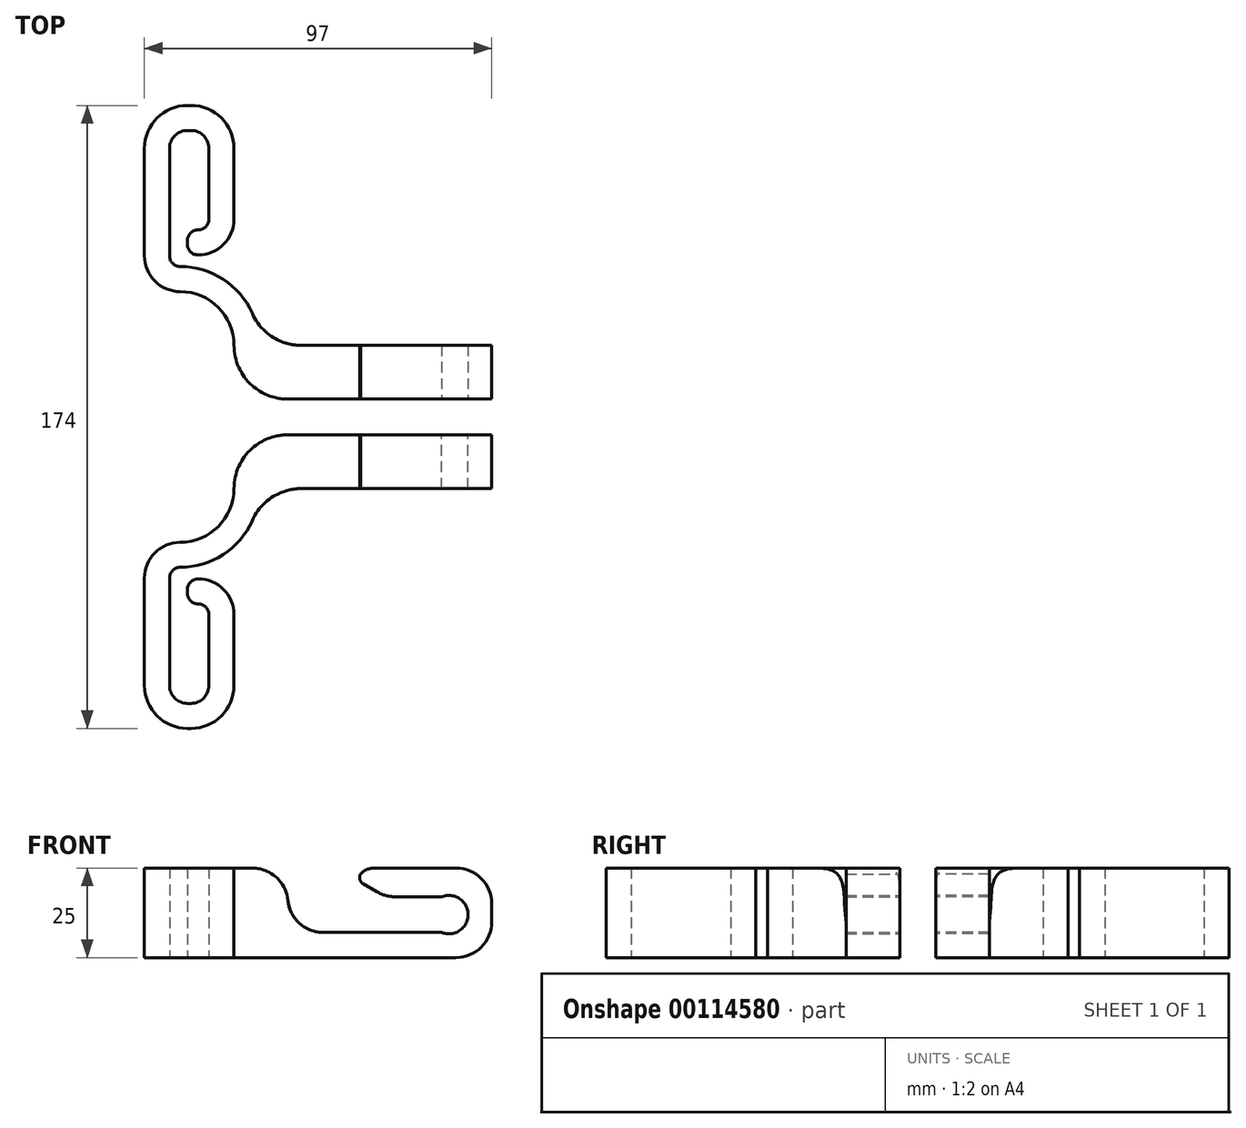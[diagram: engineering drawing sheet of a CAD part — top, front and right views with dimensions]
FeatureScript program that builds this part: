
annotation { "Feature Type Name" : "Feature", "Feature Type Description" : "" }
export const myFeature = defineFeature(function(context is Context, id is Id, definition is map)
    precondition{}
    {
        {
            var Q0;
            Q0=qCreatedBy(makeId("Top.planeOp"),FACE);
            var sketch = newSketch(context, id + "F0", { "sketchPlane" : qUnion([Q0])});
            skLineSegment(sketch, "E0", {"start": v(0, 15) * mm, "end": v(0, 15) * mm});
            skLineSegment(sketch, "E1", {"start": v(-15, 30) * mm, "end": v(-15, 30) * mm});
            skLineSegment(sketch, "E2", {"start": v(-25, 40) * mm, "end": v(-25, 70) * mm});
            skLineSegment(sketch, "E3", {"start": v(-13, 82) * mm, "end": v(-12, 82) * mm});
            skLineSegment(sketch, "E4", {"start": v(15, 0) * mm, "end": v(72, 0) * mm});
            skLineSegment(sketch, "E5", {"start": v(72, 0) * mm, "end": v(72, 15) * mm});
            skPoint(sketch, "E6.visualSharp", {"position": v(0, 30) * mm});
            skArc(sketch, "E6.filletArc", {"start": v(0, 15) * mm, "mid": v(-4.4, 25.6) * mm, "end": v(-15, 30) * mm});
            skLineSegment(sketch, "E7", {"start": v(0, 70) * mm, "end": v(0, 50.23) * mm});
            skLineSegment(sketch, "E8", {"start": v(-10, 40.23) * mm, "end": v(-10, 40.23) * mm});
            skPoint(sketch, "E9.visualSharp", {"position": v(-25, 30) * mm});
            skArc(sketch, "E9.filletArc", {"start": v(-25, 40) * mm, "mid": v(-22.07, 32.93) * mm, "end": v(-15, 30) * mm});
            skPoint(sketch, "E10.visualSharp", {"position": v(0, 40.23) * mm});
            skArc(sketch, "E10.filletArc", {"start": v(-10, 40.23) * mm, "mid": v(-2.93, 43.16) * mm, "end": v(0, 50.23) * mm});
            skPoint(sketch, "E11.visualSharp", {"position": v(0, 82) * mm});
            skArc(sketch, "E11.filletArc", {"start": v(0, 70) * mm, "mid": v(-3.51, 78.49) * mm, "end": v(-12, 82) * mm});
            skPoint(sketch, "E12.visualSharp", {"position": v(-25, 82) * mm});
            skArc(sketch, "E12.filletArc", {"start": v(-13, 82) * mm, "mid": v(-21.49, 78.49) * mm, "end": v(-25, 70) * mm});
            skArc(sketch, "E13.0", {"start": v(5.11, 23.92) * mm, "mid": v(-3, 33.44) * mm, "end": v(-15, 37) * mm});
            skArc(sketch, "E13.1", {"start": v(-18, 40) * mm, "mid": v(-17.12, 37.88) * mm, "end": v(-15, 37) * mm});
            skLineSegment(sketch, "E13.2", {"start": v(-18, 40) * mm, "end": v(-18, 70) * mm});
            skArc(sketch, "E13.3", {"start": v(-13, 75) * mm, "mid": v(-16.54, 73.54) * mm, "end": v(-18, 70) * mm});
            skLineSegment(sketch, "E13.4", {"start": v(-13, 75) * mm, "end": v(-12, 75) * mm});
            skLineSegment(sketch, "E13.5", {"start": v(-10, 47.23) * mm, "end": v(-10, 47.23) * mm});
            skArc(sketch, "E13.6", {"start": v(-10, 47.23) * mm, "mid": v(-7.88, 48.11) * mm, "end": v(-7, 50.23) * mm});
            skLineSegment(sketch, "E13.7", {"start": v(-7, 70) * mm, "end": v(-7, 50.23) * mm});
            skArc(sketch, "E13.8", {"start": v(-7, 70) * mm, "mid": v(-8.46, 73.54) * mm, "end": v(-12, 75) * mm});
            skLineSegment(sketch, "E14", {"start": v(-13, 44.23) * mm, "end": v(-13, 43.23) * mm});
            skPoint(sketch, "E15.visualSharp", {"position": v(-13, 47.23) * mm});
            skArc(sketch, "E15.filletArc", {"start": v(-10, 47.23) * mm, "mid": v(-12.12, 46.35) * mm, "end": v(-13, 44.23) * mm});
            skPoint(sketch, "E16.visualSharp", {"position": v(-13, 40.23) * mm});
            skArc(sketch, "E16.filletArc", {"start": v(-13, 43.23) * mm, "mid": v(-12.12, 41.11) * mm, "end": v(-10, 40.23) * mm});
            skLineSegment(sketch, "E17", {"start": v(72, 15) * mm, "end": v(18.82, 15) * mm});
            skPoint(sketch, "E18.visualSharp", {"position": v(0, 0) * mm});
            skArc(sketch, "E18.filletArc", {"start": v(0, 15) * mm, "mid": v(4.4, 4.4) * mm, "end": v(15, 0) * mm});
            skPoint(sketch, "E19.visualSharp", {"position": v(7, 15) * mm});
            skArc(sketch, "E19.filletArc", {"start": v(5.11, 23.92) * mm, "mid": v(10.64, 17.43) * mm, "end": v(18.82, 15) * mm});
            skSolve(sketch);
        }
        {
            var Q0;
            Q0 = qSketchRegion(id + "F0", true);
            extrude(context, id + "F1", {"entities" : qUnion([Q0]), "depth" : 25 * mm});
        }
        {
            var Q0;
            Q0=makeQuery(id+"F1.opExtrude","SWEPT_FACE",FACE,{"disambiguationData":[OSD([sQuery(id+"F0.wireOp",EDGE,"E4")])]});
            var sketch = newSketch(context, id + "F2", { "sketchPlane" : qUnion([Q0])});
            skLineSegment(sketch, "E20", {"start": v(15, 31.39) * mm, "end": v(15, 17) * mm});
            skLineSegment(sketch, "E21", {"start": v(25, 7) * mm, "end": v(60, 7) * mm});
            skLineSegment(sketch, "E22", {"start": v(65, 12) * mm, "end": v(65, 12) * mm});
            skLineSegment(sketch, "E23", {"start": v(60, 17) * mm, "end": v(45, 17) * mm});
            skLineSegment(sketch, "E24", {"start": v(40, 18.34) * mm, "end": v(36.08, 20.6) * mm});
            skLineSegment(sketch, "E25", {"start": v(35.35, 23.33) * mm, "end": v(40, 31.39) * mm});
            skLineSegment(sketch, "E26", {"start": v(40, 31.39) * mm, "end": v(15, 31.39) * mm});
            skPoint(sketch, "E27.visualSharp", {"position": v(15, 7) * mm});
            skArc(sketch, "E27.filletArc", {"start": v(15, 17) * mm, "mid": v(17.93, 9.93) * mm, "end": v(25, 7) * mm});
            skPoint(sketch, "E28.visualSharp", {"position": v(42.32, 17) * mm});
            skArc(sketch, "E28.filletArc", {"start": v(40, 18.34) * mm, "mid": v(42.41, 17.34) * mm, "end": v(45, 17) * mm});
            skPoint(sketch, "E29.visualSharp", {"position": v(65, 17) * mm});
            skArc(sketch, "E29.filletArc", {"start": v(65, 12) * mm, "mid": v(63.54, 15.54) * mm, "end": v(60, 17) * mm});
            skPoint(sketch, "E30.visualSharp", {"position": v(65, 7) * mm});
            skArc(sketch, "E30.filletArc", {"start": v(60, 7) * mm, "mid": v(63.54, 8.46) * mm, "end": v(65, 12) * mm});
            skPoint(sketch, "E31.visualSharp", {"position": v(34.35, 21.6) * mm});
            skArc(sketch, "E31.filletArc", {"start": v(35.35, 23.33) * mm, "mid": v(35.15, 21.82) * mm, "end": v(36.08, 20.6) * mm});
            skSolve(sketch);
        }
        {
            var Q0;
            Q0 = qSketchRegion(id + "F2", true);
            extrude(context, id + "F3", {"entities" : qUnion([Q0]), "operationType" : NewBodyOperationType.REMOVE, "endBound" : BoundingType.THROUGH_ALL, "oppositeDirection" : true, "depth" : 25 * mm});
        }
        {
            var Q0;
            Q0=makeQuery(id+"F1.opExtrude","SWEPT_FACE",FACE,{"disambiguationData":[OSD([sQuery(id+"F0.wireOp",EDGE,"E4")])]});
            var sketch = newSketch(context, id + "F4", { "sketchPlane" : qUnion([Q0])});
            skCircle(sketch, "E32", {"center": v(60, 12) * mm, "radius": 5.38 * mm});
            skSolve(sketch);
        }
        {
            var Q0;
            Q0 = qSketchRegion(id + "F4", true);
            extrude(context, id + "F5", {"entities" : qUnion([Q0]), "operationType" : NewBodyOperationType.REMOVE, "endBound" : BoundingType.THROUGH_ALL, "oppositeDirection" : true, "depth" : 25 * mm});
        }
        {
            var Q0;
            Q0=makeQuery(id+"F3.boolean.opBoolean","INTERSECT",EDGE,{"derivedFrom":[makeQuery(id+"F1.opExtrude","CAP_FACE",FACE,{"disambiguationData":[OSD([sQuery(id+"F0.wireOp",EDGE,"E2"),sQuery(id+"F0.wireOp",EDGE,"E3"),sQuery(id+"F0.wireOp",EDGE,"E4"),sQuery(id+"F0.wireOp",EDGE,"E5"),sQuery(id+"F0.wireOp",EDGE,"E6.filletArc"),sQuery(id+"F0.wireOp",EDGE,"E7"),sQuery(id+"F0.wireOp",EDGE,"E9.filletArc"),sQuery(id+"F0.wireOp",EDGE,"E10.filletArc"),sQuery(id+"F0.wireOp",EDGE,"E11.filletArc"),sQuery(id+"F0.wireOp",EDGE,"E12.filletArc"),sQuery(id+"F0.wireOp",EDGE,"E13.0"),sQuery(id+"F0.wireOp",EDGE,"E13.1"),sQuery(id+"F0.wireOp",EDGE,"E13.2"),sQuery(id+"F0.wireOp",EDGE,"E13.3"),sQuery(id+"F0.wireOp",EDGE,"E13.4"),sQuery(id+"F0.wireOp",EDGE,"E13.6"),sQuery(id+"F0.wireOp",EDGE,"E13.7"),sQuery(id+"F0.wireOp",EDGE,"E13.8"),sQuery(id+"F0.wireOp",EDGE,"E14"),sQuery(id+"F0.wireOp",EDGE,"E15.filletArc"),sQuery(id+"F0.wireOp",EDGE,"E16.filletArc"),sQuery(id+"F0.wireOp",EDGE,"E17"),sQuery(id+"F0.wireOp",EDGE,"E18.filletArc"),sQuery(id+"F0.wireOp",EDGE,"E19.filletArc")])],"isStart":false}),makeQuery(id+"F3.opExtrude","SWEPT_FACE",FACE,{"disambiguationData":[OSD([sQuery(id+"F2.wireOp",EDGE,"E20")])]})]});
            var Q1;
            Q1=makeQuery(id+"F1.opExtrude","CAP_EDGE",EDGE,{"disambiguationData":[OSD([sQuery(id+"F0.wireOp",EDGE,"E5")])],"isStart":false});
            var Q2;
            Q2=makeQuery(id+"F1.opExtrude","CAP_EDGE",EDGE,{"disambiguationData":[OSD([sQuery(id+"F0.wireOp",EDGE,"E5")])],"isStart":true});
            fillet(context, id + "F6", {"entities" : qUnion([Q0, Q1, Q2]), "radius" : 10 * mm, "tangentPropagation" : true, "allowEdgeOverflow" : false});
        }
        {
            var Q0;
            Q0=makeQuery(id+"F3.boolean.opBoolean","INTERSECT",EDGE,{"derivedFrom":[makeQuery(id+"F1.opExtrude","CAP_FACE",FACE,{"disambiguationData":[OSD([sQuery(id+"F0.wireOp",EDGE,"E2"),sQuery(id+"F0.wireOp",EDGE,"E3"),sQuery(id+"F0.wireOp",EDGE,"E4"),sQuery(id+"F0.wireOp",EDGE,"E5"),sQuery(id+"F0.wireOp",EDGE,"E6.filletArc"),sQuery(id+"F0.wireOp",EDGE,"E7"),sQuery(id+"F0.wireOp",EDGE,"E9.filletArc"),sQuery(id+"F0.wireOp",EDGE,"E10.filletArc"),sQuery(id+"F0.wireOp",EDGE,"E11.filletArc"),sQuery(id+"F0.wireOp",EDGE,"E12.filletArc"),sQuery(id+"F0.wireOp",EDGE,"E13.0"),sQuery(id+"F0.wireOp",EDGE,"E13.1"),sQuery(id+"F0.wireOp",EDGE,"E13.2"),sQuery(id+"F0.wireOp",EDGE,"E13.3"),sQuery(id+"F0.wireOp",EDGE,"E13.4"),sQuery(id+"F0.wireOp",EDGE,"E13.6"),sQuery(id+"F0.wireOp",EDGE,"E13.7"),sQuery(id+"F0.wireOp",EDGE,"E13.8"),sQuery(id+"F0.wireOp",EDGE,"E14"),sQuery(id+"F0.wireOp",EDGE,"E15.filletArc"),sQuery(id+"F0.wireOp",EDGE,"E16.filletArc"),sQuery(id+"F0.wireOp",EDGE,"E17"),sQuery(id+"F0.wireOp",EDGE,"E18.filletArc"),sQuery(id+"F0.wireOp",EDGE,"E19.filletArc")])],"isStart":false}),makeQuery(id+"F3.opExtrude","SWEPT_FACE",FACE,{"disambiguationData":[OSD([sQuery(id+"F2.wireOp",EDGE,"E25")])]})]});
            fillet(context, id + "F7", {"entities" : qUnion([Q0]), "radius" : 5 * mm, "tangentPropagation" : true, "allowEdgeOverflow" : false});
        }
        {
            var Q0;
            Q0=makeQuery(id+"F1.opExtrude","SWEPT_FACE",FACE,{"disambiguationData":[OSD([sQuery(id+"F0.wireOp",EDGE,"E4")])]});
            cPlane(context, id + "F8", {"entities" : qUnion([Q0]), "cplaneType" : CPlaneType.OFFSET, "offset" : 5 * mm, "width" : 150 * mm, "height" : 150 * mm});
        }
        {
            var Q0;
            Q0=makeQuery(id+"F1.opExtrude","SWEPT_BODY",BODY,{"disambiguationData":[OSD([sQuery(id+"F0.wireOp",EDGE,"E2"),sQuery(id+"F0.wireOp",EDGE,"E3"),sQuery(id+"F0.wireOp",EDGE,"E4"),sQuery(id+"F0.wireOp",EDGE,"E5"),sQuery(id+"F0.wireOp",EDGE,"E6.filletArc"),sQuery(id+"F0.wireOp",EDGE,"E7"),sQuery(id+"F0.wireOp",EDGE,"E9.filletArc"),sQuery(id+"F0.wireOp",EDGE,"E10.filletArc"),sQuery(id+"F0.wireOp",EDGE,"E11.filletArc"),sQuery(id+"F0.wireOp",EDGE,"E12.filletArc"),sQuery(id+"F0.wireOp",EDGE,"E13.0"),sQuery(id+"F0.wireOp",EDGE,"E13.1"),sQuery(id+"F0.wireOp",EDGE,"E13.2"),sQuery(id+"F0.wireOp",EDGE,"E13.3"),sQuery(id+"F0.wireOp",EDGE,"E13.4"),sQuery(id+"F0.wireOp",EDGE,"E13.6"),sQuery(id+"F0.wireOp",EDGE,"E13.7"),sQuery(id+"F0.wireOp",EDGE,"E13.8"),sQuery(id+"F0.wireOp",EDGE,"E14"),sQuery(id+"F0.wireOp",EDGE,"E15.filletArc"),sQuery(id+"F0.wireOp",EDGE,"E16.filletArc"),sQuery(id+"F0.wireOp",EDGE,"E17"),sQuery(id+"F0.wireOp",EDGE,"E18.filletArc"),sQuery(id+"F0.wireOp",EDGE,"E19.filletArc")])]});
            var Q1;
            Q1=qCreatedBy(id+"F8.planeOp",FACE);
            mirror(context, id + "F9", {"entities" : qUnion([Q0]), "mirrorPlane" : qUnion([Q1])});
        }
    });
